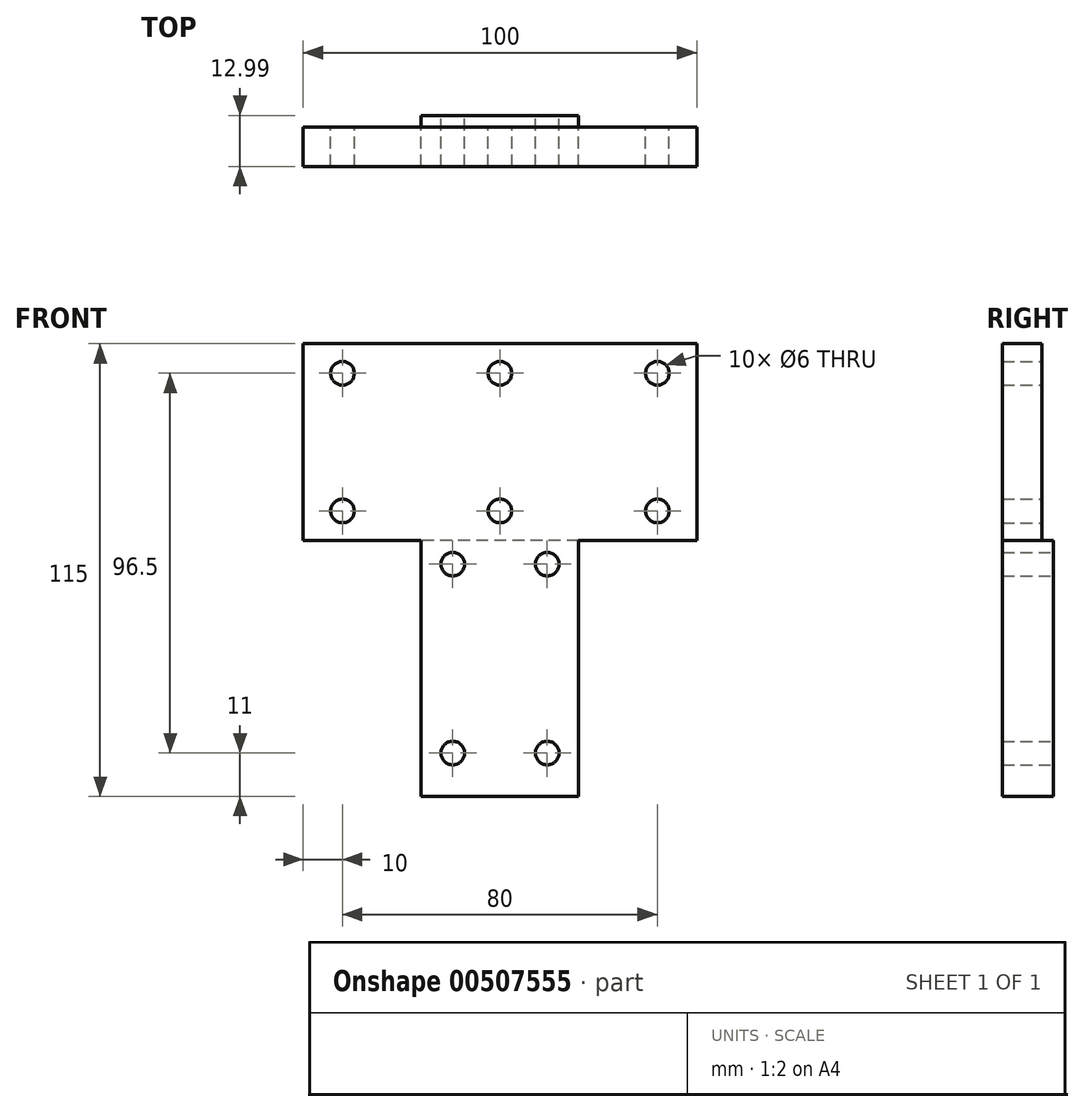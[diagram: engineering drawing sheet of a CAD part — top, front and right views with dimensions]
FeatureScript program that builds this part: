
annotation { "Feature Type Name" : "Feature", "Feature Type Description" : "" }
export const myFeature = defineFeature(function(context is Context, id is Id, definition is map)
    precondition{}
    {
        {
            var Q0;
            Q0=qCreatedBy(makeId("Front.planeOp"),FACE);
            var sketch = newSketch(context, id + "F0", { "sketchPlane" : qUnion([Q0])});
            skLineSegment(sketch, "E0.bottom", {"start": v(30, 0) * mm, "end": v(70, 0) * mm});
            skLineSegment(sketch, "E0.top", {"start": v(0, 115) * mm, "end": v(100, 115) * mm});
            skLineSegment(sketch, "E0.left", {"start": v(0, 65) * mm, "end": v(0, 115) * mm});
            skLineSegment(sketch, "E0.right", {"start": v(100, 65) * mm, "end": v(100, 115) * mm});
            skLineSegment(sketch, "E1.top", {"start": v(0, 65) * mm, "end": v(30, 65) * mm});
            skLineSegment(sketch, "E1.right", {"start": v(30, 0) * mm, "end": v(30, 65) * mm});
            skLineSegment(sketch, "E2.top", {"start": v(100, 65) * mm, "end": v(70, 65) * mm});
            skLineSegment(sketch, "E2.right", {"start": v(70, 0) * mm, "end": v(70, 65) * mm});
            skCircle(sketch, "E3", {"center": v(10, 107.5) * mm, "radius": 3 * mm});
            skCircle(sketch, "E4", {"center": v(10, 72.5) * mm, "radius": 3 * mm});
            skCircle(sketch, "E5", {"center": v(50, 107.5) * mm, "radius": 3 * mm});
            skCircle(sketch, "E6", {"center": v(50, 72.5) * mm, "radius": 3 * mm});
            skCircle(sketch, "E7", {"center": v(90, 107.5) * mm, "radius": 3 * mm});
            skCircle(sketch, "E8", {"center": v(90, 72.5) * mm, "radius": 3 * mm});
            skCircle(sketch, "E9", {"center": v(38, 11) * mm, "radius": 3 * mm});
            skCircle(sketch, "E10", {"center": v(38, 59) * mm, "radius": 3 * mm});
            skCircle(sketch, "E11", {"center": v(62, 59) * mm, "radius": 3 * mm});
            skCircle(sketch, "E12", {"center": v(62, 11) * mm, "radius": 3 * mm});
            skSolve(sketch);
        }
        {
            var Q0;
            Q0=makeQuery(id+"F0.imprint","IMPRINT",FACE,{"disambiguationData":[TD([[makeQuery(id+"F0.imprint","IMPRINT",EDGE,{"derivedFrom":sQuery(id+"F0.wireOp",EDGE,"E0.bottom")}),1.0]])]});
            extrude(context, id + "F1", {"entities" : qUnion([Q0]), "depth" : 10 * mm, "offsetDistance" : 25 * mm});
        }
        {
            var Q0;
            Q0=makeQuery(id+"F1.opExtrude","CAP_FACE",FACE,{"disambiguationData":[OSD([sQuery(id+"F0.wireOp",EDGE,"E0.bottom"),sQuery(id+"F0.wireOp",EDGE,"E0.top"),sQuery(id+"F0.wireOp",EDGE,"E0.left"),sQuery(id+"F0.wireOp",EDGE,"E0.right"),sQuery(id+"F0.wireOp",EDGE,"E1.top"),sQuery(id+"F0.wireOp",EDGE,"E1.right"),sQuery(id+"F0.wireOp",EDGE,"E2.top"),sQuery(id+"F0.wireOp",EDGE,"E2.right"),sQuery(id+"F0.wireOp",EDGE,"E3"),sQuery(id+"F0.wireOp",EDGE,"E4"),sQuery(id+"F0.wireOp",EDGE,"E5"),sQuery(id+"F0.wireOp",EDGE,"E6"),sQuery(id+"F0.wireOp",EDGE,"E7"),sQuery(id+"F0.wireOp",EDGE,"E8"),sQuery(id+"F0.wireOp",EDGE,"E9"),sQuery(id+"F0.wireOp",EDGE,"E10"),sQuery(id+"F0.wireOp",EDGE,"E11"),sQuery(id+"F0.wireOp",EDGE,"E12")])],"isStart":true});
            var sketch = newSketch(context, id + "F2", { "sketchPlane" : qUnion([Q0])});
            skLineSegment(sketch, "E13.bottom", {"start": v(-70, 0) * mm, "end": v(-30, 0) * mm});
            skLineSegment(sketch, "E13.top", {"start": v(-70, 65) * mm, "end": v(-30, 65) * mm});
            skLineSegment(sketch, "E13.left", {"start": v(-70, 0) * mm, "end": v(-70, 65) * mm});
            skLineSegment(sketch, "E13.right", {"start": v(-30, 0) * mm, "end": v(-30, 65) * mm});
            skSolve(sketch);
        }
        {
            var Q0;
            Q0=makeQuery(id+"F2.imprint","IMPRINT",FACE,{"disambiguationData":[TD([[makeQuery(id+"F2.imprint","IMPRINT",EDGE,{"derivedFrom":sQuery(id+"F2.wireOp",EDGE,"E13.bottom")}),-1.0]])]});
            extrude(context, id + "F3", {"entities" : qUnion([Q0]), "operationType" : NewBodyOperationType.ADD, "depth" : 3 * mm, "offsetDistance" : 25 * mm});
        }
    });
